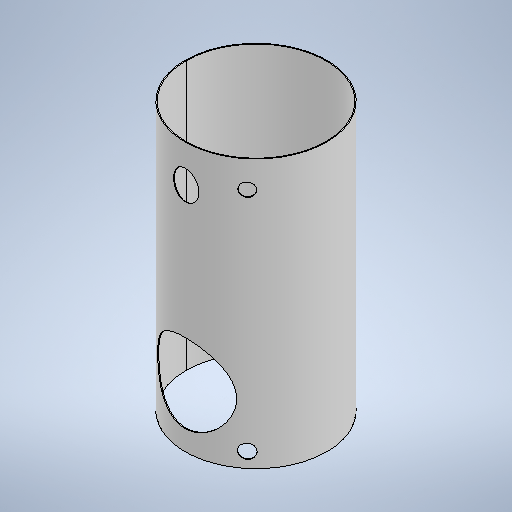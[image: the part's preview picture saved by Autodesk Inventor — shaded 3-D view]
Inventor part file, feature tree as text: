
AUTODESK INVENTOR PART (.ipt)
format: ipt  version: 2025.1 (Build 291241020, 241B)  size: 439,808 bytes
history: native  units: mm
features: sketch x6, extrude x3, plane x3, revolve x1, other x1
ambient origin geometry x8: Origin, YZ Plane, XZ Plane, XY Plane, X Axis, Y Axis, Z Axis, Center Point
bodies: Solid1 (feature_tree)
feature tree (14):
  revolve  "Revolution1"  [1 undecoded]
  extrude  "Extrusion1"  Depth=62.8144mm
  sketch  "Sketch3"  dims[d4=530.0mm d10=0.0mm d11=0.0mm]
  plane  "Work Plane2"
  extrude  "Extrusion2"  TaperAngle=0.0deg  [1 undecoded]
  plane  "Work Plane3"
  sketch  "Sketch5"  dims[d16=400.0mm]
  plane  "Work Plane4"
  extrude  "Extrusion3"  Depth=400.0mm
  sketch  "Sketch1"  dims[d0=6.0mm d1=1802.296908mm]
  sketch  "Sketch2"  dims[d2=940.0mm d3=62.8144mm]
  sketch  "Sketch4"  dims[d12=400.0mm d15=200.0mm]
  sketch  "Sketch6"  dims[d17=180.0mm d18=8.726646mm d19=90.0mm d20=100.0mm d21=1622.296908mm d22=0.0mm d23=0.0mm d24=180.0mm d26=0.0mm d27=30.0deg d28=250.0mm d29=170.0mm d30=0.0mm d31=0.0mm]
  other  "Definition1"
note: 2 required parameter values undecoded (feature->parameter linkage not recoverable at this tier; creation-order binding heuristic only, values carry confidence <= 0.55)